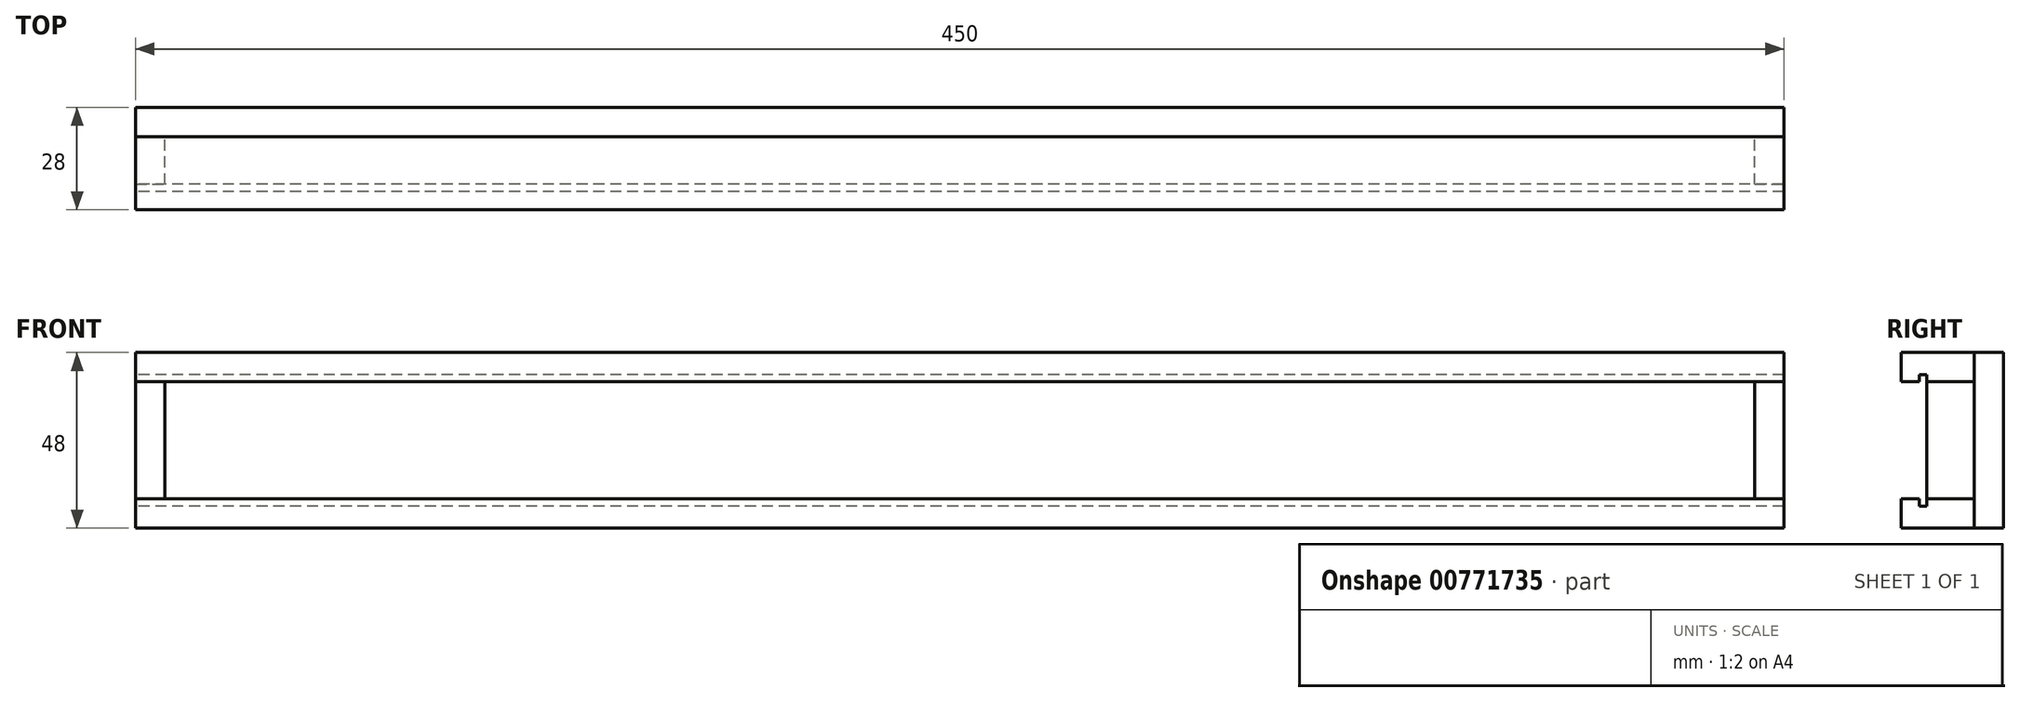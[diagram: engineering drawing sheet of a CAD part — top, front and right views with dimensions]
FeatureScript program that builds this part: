
annotation { "Feature Type Name" : "Feature", "Feature Type Description" : "" }
export const myFeature = defineFeature(function(context is Context, id is Id, definition is map)
    precondition{}
    {
        {
            assignVariable(context, id + "F0", {"name" : "MatrixWidth", "anyValue" : 128});
        }
        {
            assignVariable(context, id + "F1", {"name" : "Thickness", "anyValue" : 8});
        }
        {
            var Q0;
            Q0=qCreatedBy(makeId("Front.planeOp"),FACE);
            var sketch = newSketch(context, id + "F2", { "sketchPlane" : qUnion([Q0])});
            skLineSegment(sketch, "E0.bottom", {"start": v(217, 16) * mm, "end": v(-217, 16) * mm});
            skLineSegment(sketch, "E0.top", {"start": v(217, -16) * mm, "end": v(-217, -16) * mm});
            skLineSegment(sketch, "E0.left", {"start": v(217, 16) * mm, "end": v(217, -16) * mm});
            skLineSegment(sketch, "E0.right", {"start": v(-217, 16) * mm, "end": v(-217, -16) * mm});
            skPoint(sketch, "E0.middle", {"position": v(0, 0) * mm});
            skLineSegment(sketch, "E1.0", {"start": v(-225, 16) * mm, "end": v(-225, -16) * mm});
            skLineSegment(sketch, "E2", {"start": v(-225, 16) * mm, "end": v(-217, 16) * mm});
            skLineSegment(sketch, "E3", {"start": v(-225, -16) * mm, "end": v(-217, -16) * mm});
            skLineSegment(sketch, "E4.0", {"start": v(225, 16) * mm, "end": v(225, -16) * mm});
            skLineSegment(sketch, "E5", {"start": v(217, 16) * mm, "end": v(225, 16) * mm});
            skLineSegment(sketch, "E6", {"start": v(217, -16) * mm, "end": v(225, -16) * mm});
            skLineSegment(sketch, "E7.0", {"start": v(-225, -24) * mm, "end": v(-217, -24) * mm});
            skLineSegment(sketch, "E7.1", {"start": v(217, -24) * mm, "end": v(-217, -24) * mm});
            skLineSegment(sketch, "E7.2", {"start": v(217, -24) * mm, "end": v(225, -24) * mm});
            skLineSegment(sketch, "E8", {"start": v(-225, -24) * mm, "end": v(-225, -16) * mm});
            skLineSegment(sketch, "E9", {"start": v(225, -24) * mm, "end": v(225, -16) * mm});
            skLineSegment(sketch, "E10.0", {"start": v(217, 24) * mm, "end": v(225, 24) * mm});
            skLineSegment(sketch, "E10.1", {"start": v(217, 24) * mm, "end": v(-217, 24) * mm});
            skLineSegment(sketch, "E10.2", {"start": v(-225, 24) * mm, "end": v(-217, 24) * mm});
            skLineSegment(sketch, "E11", {"start": v(-225, 16) * mm, "end": v(-225, 24) * mm});
            skLineSegment(sketch, "E12", {"start": v(225, 16) * mm, "end": v(225, 24) * mm});
            skSolve(sketch);
        }
        {
            var Q0;
            Q0=makeQuery(id+"F2.imprint","IMPRINT",FACE,{"disambiguationData":[TD([[makeQuery(id+"F2.imprint","IMPRINT",EDGE,{"derivedFrom":sQuery(id+"F2.wireOp",EDGE,"E0.bottom")}),-1.0]])]});
            extrude(context, id + "F3", {"entities" : qUnion([Q0]), "depth" : 20 * mm, "offsetDistance" : 25 * mm});
        }
        {
            var Q0;
            Q0=makeQuery(id+"F2.imprint","IMPRINT",FACE,{"disambiguationData":[TD([[makeQuery(id+"F2.imprint","IMPRINT",EDGE,{"derivedFrom":sQuery(id+"F2.wireOp",EDGE,"E0.right")}),-1.0]])]});
            var Q1;
            Q1=makeQuery(id+"F2.imprint","IMPRINT",FACE,{"disambiguationData":[TD([[makeQuery(id+"F2.imprint","IMPRINT",EDGE,{"derivedFrom":sQuery(id+"F2.wireOp",EDGE,"E0.left")}),1.0]])]});
            extrude(context, id + "F4", {"entities" : qUnion([Q0, Q1]), "depth" : 13 * mm, "offsetDistance" : 25 * mm});
        }
        {
            var Q0;
            Q0=makeQuery(id+"F2.imprint","IMPRINT",FACE,{"disambiguationData":[TD([[makeQuery(id+"F2.imprint","IMPRINT",EDGE,{"derivedFrom":sQuery(id+"F2.wireOp",EDGE,"E0.bottom")}),1.0]])]});
            var Q1;
            Q1=makeQuery(id+"F2.imprint","IMPRINT",FACE,{"disambiguationData":[TD([[makeQuery(id+"F2.imprint","IMPRINT",EDGE,{"derivedFrom":sQuery(id+"F2.wireOp",EDGE,"E0.top")}),1.0]])]});
            var Q2;
            Q2=makeQuery(id+"F2.imprint","IMPRINT",FACE,{"disambiguationData":[TD([[makeQuery(id+"F2.imprint","IMPRINT",EDGE,{"derivedFrom":sQuery(id+"F2.wireOp",EDGE,"E0.left")}),1.0]])]});
            var Q3;
            Q3=makeQuery(id+"F2.imprint","IMPRINT",FACE,{"disambiguationData":[TD([[makeQuery(id+"F2.imprint","IMPRINT",EDGE,{"derivedFrom":sQuery(id+"F2.wireOp",EDGE,"E0.bottom")}),-1.0]])]});
            var Q4;
            Q4=makeQuery(id+"F2.imprint","IMPRINT",FACE,{"disambiguationData":[TD([[makeQuery(id+"F2.imprint","IMPRINT",EDGE,{"derivedFrom":sQuery(id+"F2.wireOp",EDGE,"E0.right")}),-1.0]])]});
            extrude(context, id + "F5", {"entities" : qUnion([Q0, Q1, Q2, Q3, Q4]), "oppositeDirection" : true, "depth" : (getVariable(context, 'Thickness')) * mm, "offsetDistance" : 25 * mm});
        }
        {
            var Q0;
            Q0=makeQuery(id+"F3.opExtrude","SWEPT_FACE",FACE,{"disambiguationData":[OSD([sQuery(id+"F2.wireOp",EDGE,"E11")])]});
            var sketch = newSketch(context, id + "F6", { "sketchPlane" : qUnion([Q0])});
            skLineSegment(sketch, "E13.bottom", {"start": v(0, 24) * mm, "end": v(20, 24) * mm});
            skLineSegment(sketch, "E13.top", {"start": v(0, 16) * mm, "end": v(20, 16) * mm});
            skLineSegment(sketch, "E13.left", {"start": v(0, 24) * mm, "end": v(0, 16) * mm});
            skLineSegment(sketch, "E13.right", {"start": v(20, 24) * mm, "end": v(20, 16) * mm});
            skLineSegment(sketch, "E14", {"start": v(15, 16) * mm, "end": v(15, 18) * mm});
            skLineSegment(sketch, "E15", {"start": v(13, 18) * mm, "end": v(15, 18) * mm});
            skLineSegment(sketch, "E16", {"start": v(13, 18) * mm, "end": v(13, 16) * mm});
            skSolve(sketch);
        }
        {
            var Q0;
            {var subQ0=sQuery(id+"F6.wireOp",EDGE,"E14");Q0=makeQuery(id+"F6.imprint","IMPRINT",FACE,{"disambiguationData":[TD([[makeQuery(id+"F6.imprint","IMPRINT",EDGE,{"derivedFrom":subQ0}),1.0]])]});}
            extrude(context, id + "F7", {"entities" : qUnion([Q0]), "operationType" : NewBodyOperationType.REMOVE, "oppositeDirection" : true, "depth" : (getVariable(context, 'MatrixWidth') * 3 + getVariable(context, 'Thickness') * 250) * mm, "offsetDistance" : 25 * mm});
        }
        {
            var Q0;
            Q0=makeQuery(id+"F3.opExtrude","SWEPT_BODY",BODY,{"disambiguationData":[OSD([sQuery(id+"F2.wireOp",EDGE,"E0.bottom"),sQuery(id+"F2.wireOp",EDGE,"E2"),sQuery(id+"F2.wireOp",EDGE,"E5"),sQuery(id+"F2.wireOp",EDGE,"E10.0"),sQuery(id+"F2.wireOp",EDGE,"E10.1"),sQuery(id+"F2.wireOp",EDGE,"E10.2"),sQuery(id+"F2.wireOp",EDGE,"E11"),sQuery(id+"F2.wireOp",EDGE,"E12")])]});
            var Q1;
            Q1=qCreatedBy(makeId("Top.planeOp"),FACE);
            mirror(context, id + "F8", {"entities" : qUnion([Q0]), "mirrorPlane" : qUnion([Q1])});
        }
    });
